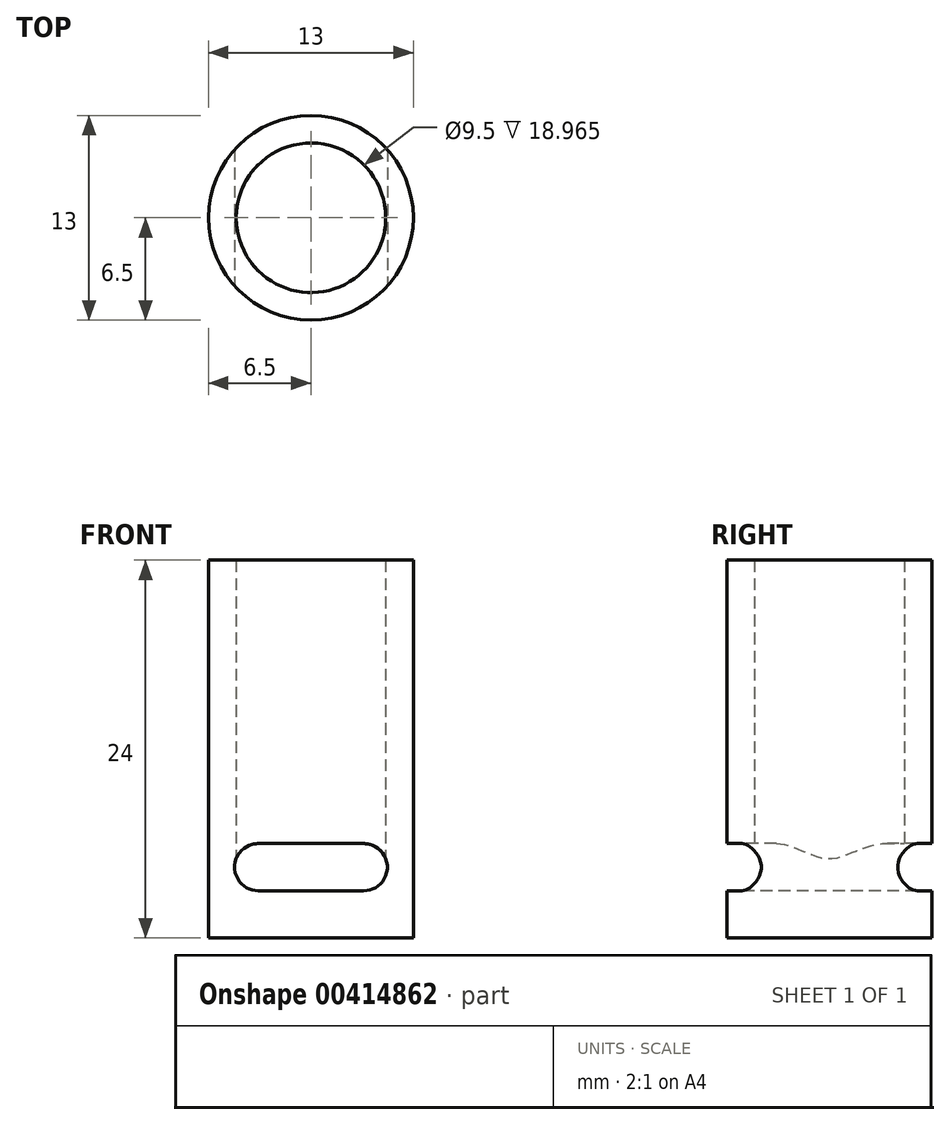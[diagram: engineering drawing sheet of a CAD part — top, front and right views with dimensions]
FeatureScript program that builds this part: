
annotation { "Feature Type Name" : "Feature", "Feature Type Description" : "" }
export const myFeature = defineFeature(function(context is Context, id is Id, definition is map)
    precondition{}
    {
        {
            var Q0;
            Q0=qCreatedBy(makeId("Top.planeOp"),FACE);
            var sketch = newSketch(context, id + "F0", { "sketchPlane" : qUnion([Q0])});
            skCircle(sketch, "E0", {"center": v(0, 0) * mm, "radius": 6.5 * mm});
            skSolve(sketch);
        }
        {
            var Q0;
            Q0 = qSketchRegion(id + "F0", true);
            extrude(context, id + "F1", {"entities" : qUnion([Q0]), "depth" : 4 * mm});
        }
        {
            var Q0;
            Q0=makeQuery(id+"F1.opExtrude","CAP_FACE",FACE,{"disambiguationData":[OSD([sQuery(id+"F0.wireOp",EDGE,"E0")])],"isStart":false});
            var sketch = newSketch(context, id + "F2", { "sketchPlane" : qUnion([Q0])});
            skCircle(sketch, "E1", {"center": v(0, 0) * mm, "radius": 4.75 * mm});
            skSolve(sketch);
        }
        {
            var Q0;
            Q0=makeQuery(id+"F2.imprint","IMPRINT",FACE,{"disambiguationData":[TD([[makeQuery(id+"F2.imprint","IMPRINT",EDGE,{"derivedFrom":sQuery(id+"F2.wireOp",EDGE,"E1")}),-1.0]])]});
            extrude(context, id + "F3", {"entities" : qUnion([Q0]), "operationType" : NewBodyOperationType.ADD, "depth" : 20 * mm});
        }
        {
            var Q0;
            Q0=qCreatedBy(makeId("Front.planeOp"),FACE);
            cPlane(context, id + "F4", {"entities" : qUnion([Q0]), "cplaneType" : CPlaneType.OFFSET, "offset" : 10 * mm, "width" : 150 * mm, "height" : 150 * mm});
        }
        {
            var Q0;
            Q0=qCreatedBy(id+"F4.planeOp",FACE);
            var sketch = newSketch(context, id + "F5", { "sketchPlane" : qUnion([Q0])});
            skLineSegment(sketch, "E2.bottom", {"start": v(-3.35, 6) * mm, "end": v(3.35, 6) * mm});
            skLineSegment(sketch, "E2.top", {"start": v(-3.35, 3) * mm, "end": v(3.35, 3) * mm});
            skLineSegment(sketch, "E2.left", {"start": v(-3.35, 6) * mm, "end": v(-3.35, 3) * mm});
            skLineSegment(sketch, "E2.right", {"start": v(3.35, 6) * mm, "end": v(3.35, 3) * mm});
            skLineSegment(sketch, "E3", {"start": v(0, 0) * mm, "end": v(0, 11.71) * mm, "construction": true});
            skPoint(sketch, "E4", {"position": v(0, 3) * mm});
            skCircle(sketch, "E5", {"center": v(3.35, 4.5) * mm, "radius": 1.5 * mm});
            skCircle(sketch, "E6", {"center": v(-3.35, 4.5) * mm, "radius": 1.5 * mm});
            skSolve(sketch);
        }
        {
            var Q0;
            Q0 = qSketchRegion(id + "F5", true);
            extrude(context, id + "F6", {"entities" : qUnion([Q0]), "operationType" : NewBodyOperationType.REMOVE, "oppositeDirection" : true, "depth" : 25 * mm});
        }
    });
